# Revit family: MB-1012-AIB
name_source: partatom
category: Plumbing Fixtures
units: mm (PartAtom-declared; Revit-internal decimal feet)

## family parameters
Always vertical = Yes
Cut with Voids When Loaded = No
OmniClass Number = 23.45.00.00
OmniClass Title = Sanitary, Laundry, and Cleaning Equipment
Part Type = Normal
Room Calculation Point = No
Round Connector Dimension = Use Diameter
Shared = No
Work Plane-Based = No

## types (1)
- MB-1012-AI
    Air Flow = 101.7 m³/h
    Air Temperature to 4" = 55 °C
    Air Velocity = 90.0 m/s
    Automatic Shut Off = 60.0 s
    Certification = http://www.helvex.com.mx
    Current Consumption = 8 A
    Default Elevation = 0"
    Description = Turbo Hand Dryer
    Documentation = http://www.helvex.com.mx
    Drying Time = 15.0 s
    Electrical Protection = Restored Auto Thermostat Engin Blows at 105° C Thermal Fuse With Court to 139° C
    Instructive = http://www.helvex.com.mx
    Manufacturer = HELVEX
    Model = MB-1012
    Noise = 78 dB
    Power Consumption = 1000 W
    Range Of Activation = Self-Adjusting 180 mm Max.
    Stainless Steel = Stainless Steel
    Total Height = 7"
    Total Length = 10"
    Total Width = 5"
    Type Comments = Electronic Line
    URL = http://www.helvex.com.mx
    Voltage = 120 V
    Voltage 2 = 60

note: source unit labels omitted for Voltage 2 — the stored unit's dimension contradicts the parameter name (converter mislabeling)

## geometry (parser evidence)
native form markers: Sweep x2
no freeform markers — native parametric forms only
